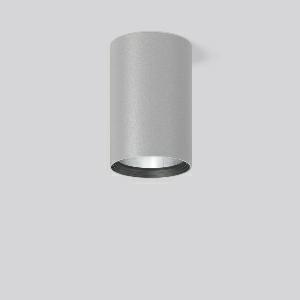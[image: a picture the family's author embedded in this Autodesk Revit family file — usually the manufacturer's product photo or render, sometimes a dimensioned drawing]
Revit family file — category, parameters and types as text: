
# Revit family: heledon_maxi_a_931218_004_1_76_95ed
name_source: partatom
category: Lighting Fixtures
units: mm (PartAtom-declared; Revit-internal decimal feet)

## family parameters
Cut with Voids When Loaded = No
Host = Face
Light Source = No
Part Type = Normal
Room Calculation Point = No
Round Connector Dimension = Use Diameter
Shared = No

## types (1)
- HELEDON maxi A (1 x LED Modul 940, 3500 lm, 4000)
    Apparent Load = 25 VA
    Approval mark = CE
    CIE Flux Codes = 100 100 100 100 100
    Color Rendering = 92
    Color Temperature = 4000
    Default Elevation = 1800 mm
    Description = Series: HELEDON maxi
Cylindrical surface-mounted downlight. Housing: die-cast aluminium, powder-coated. Internal ceiling frame polycarbonate with bayonet mounting. Black plastic ring and recessed LED to prevent glare from the side. Optical assembly with reflector made of MIRO-Silver with 98% total light reflection for outstanding efficiency - can be changed without tools. Best colour rendering index Ra>90. Suitable for Ceiling mounting. Easy installation with a separate ceiling frame with bayonet mounting and plug connection. Driver integrated. Connected via plug-in connector. High quality converter without flickering and stroboscopic effect. The following accessories can be mounted without use of tools: interchangeable lenses, decorative glasses, honeycomb louvre, clear and frosted diffusers, white interchangeable plastic ring. 
Colour: silver
Diameter: 123 mm
Height: 183 mm
Lamp: LED
Socket: without socket
Colour temperature: 4000K
Colour rendering index (CRI): 92
System power: 25 W
Rated luminous flux: 3500 lm
Luminous efficiency: 140 lm/W
Control gear: Converter, dimmable, DALI
Protection class: I
Type of protection: IP 20
    Height = 183 mm
    Lamp = 1 x LED Modul 940
    Lamp Light Flux = 3500 lm
    Lamp count = 1
    Length = 123 mm
    Lifetime = 50000 h
    Luminous efficacy = 140 lm/W
    Manufacturer = RZB
    ModVariant = No
    Model = 931218.004.1.76
    Mounting Place = Ceiling
    Mounting Type = Surface mounted
    Number of Poles = 1
    OnlyDefault = Yes
    Power Factor = 1
    Product Name = HELEDON maxi A
    Product group = Surface mounted downlights
    ProductGroupID = 302
    Protection Class = Protection class I
    Protection Degree = IP 20
    RLX_Detail_Level = 1
    RLX_Emergency_Light_Flux = 0 lm
    RLX_Emergency_Type = 0
    RLX_Emergency_Type_DB = No
    RlxData = <blob elided: 100781 chars, md5=476a00ad>
    Socket = socket
    Standby Power = 0 W
    System Light Flux = 3500 lm
    System Power = 25 W
    Type Comments = Product without accessories
    Type Image = 931192.004.jpg
    URL = http://relux.com
    VarID = ---
    Voltage = 230 V
    Voltage Range = 220-240 V
    Weight = 0.00 kg
    Width = 0 mm  [stored 0 ft]

note: [stored X ft] marks values corroborated as IEEE doubles in the binary element streams (Revit-internal decimal feet)

## geometry (parser evidence)
native form markers: Blend x4, Sweep x10
no freeform markers — native parametric forms only
